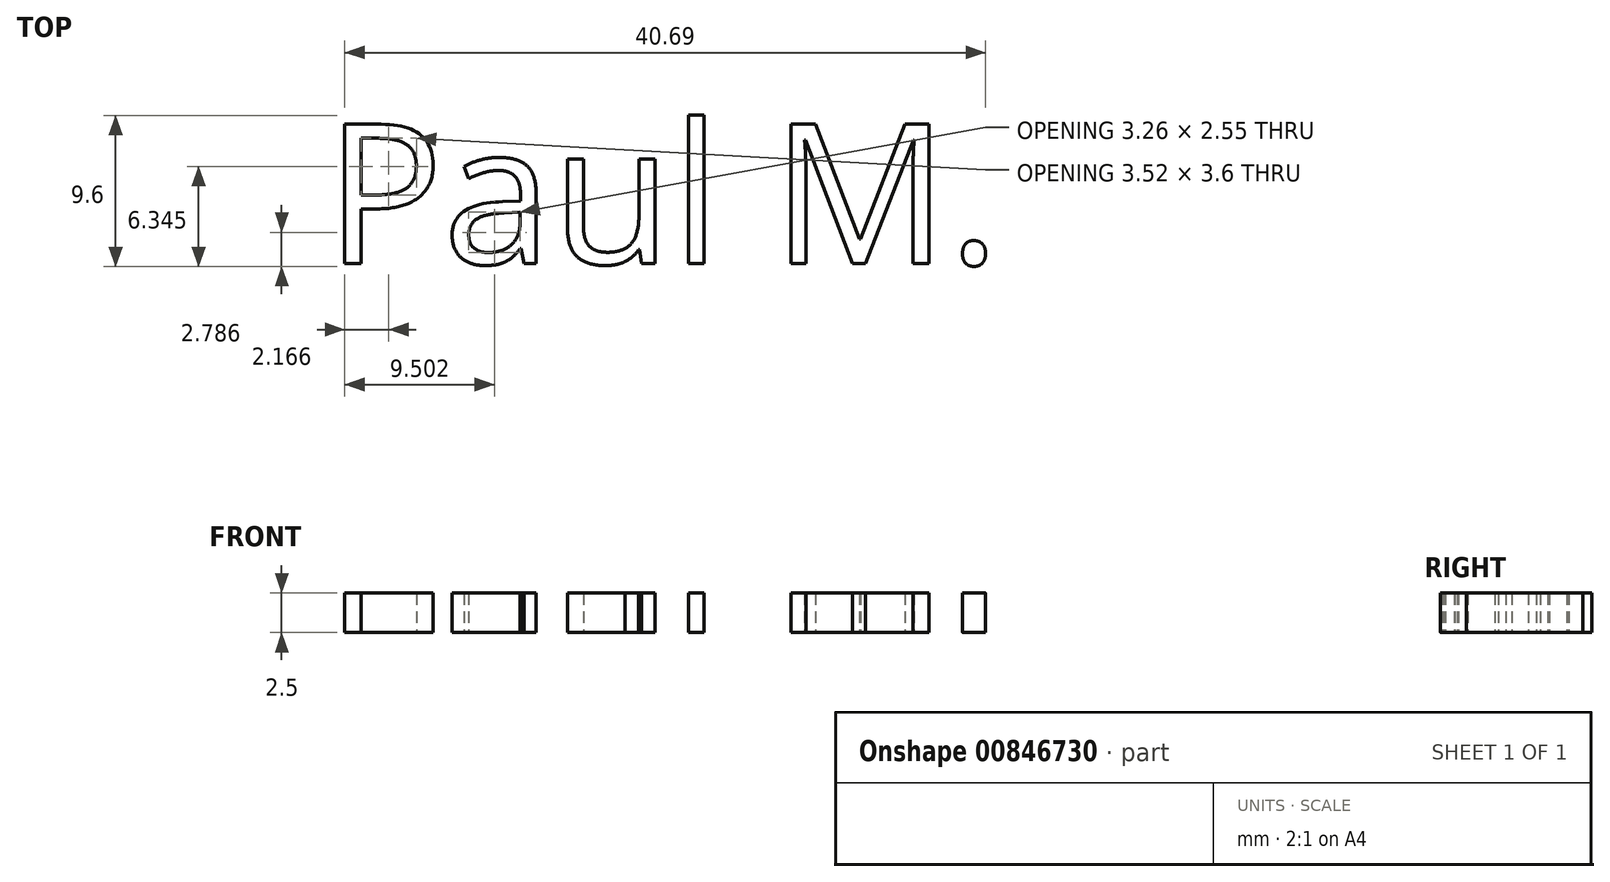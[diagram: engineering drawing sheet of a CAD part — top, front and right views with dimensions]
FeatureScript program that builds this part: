
annotation { "Feature Type Name" : "Feature", "Feature Type Description" : "" }
export const myFeature = defineFeature(function(context is Context, id is Id, definition is map)
    precondition{}
    {
        {
            var Q0;
            Q0=qCreatedBy(makeId("Top.planeOp"),FACE);
            var sketch = newSketch(context, id + "F0", { "sketchPlane" : qUnion([Q0])});
            skText(sketch, "E0", { "text": "Paul M.\n", "fontName": "OpenSans-Regular.ttf"});
            const initialGuessF0  = {"E0": [-0.0427, -0.00893, 1, 0, 0.00893]};
            skSetInitialGuess(sketch, initialGuessF0);
            skSolve(sketch);
        }
        {
            var Q0;
            Q0 = qSketchRegion(id + "F0", true);
            extrude(context, id + "F1", {"entities" : qUnion([Q0]), "depth" : 2.5 * mm, "offsetDistance" : 25 * mm});
        }
    });
